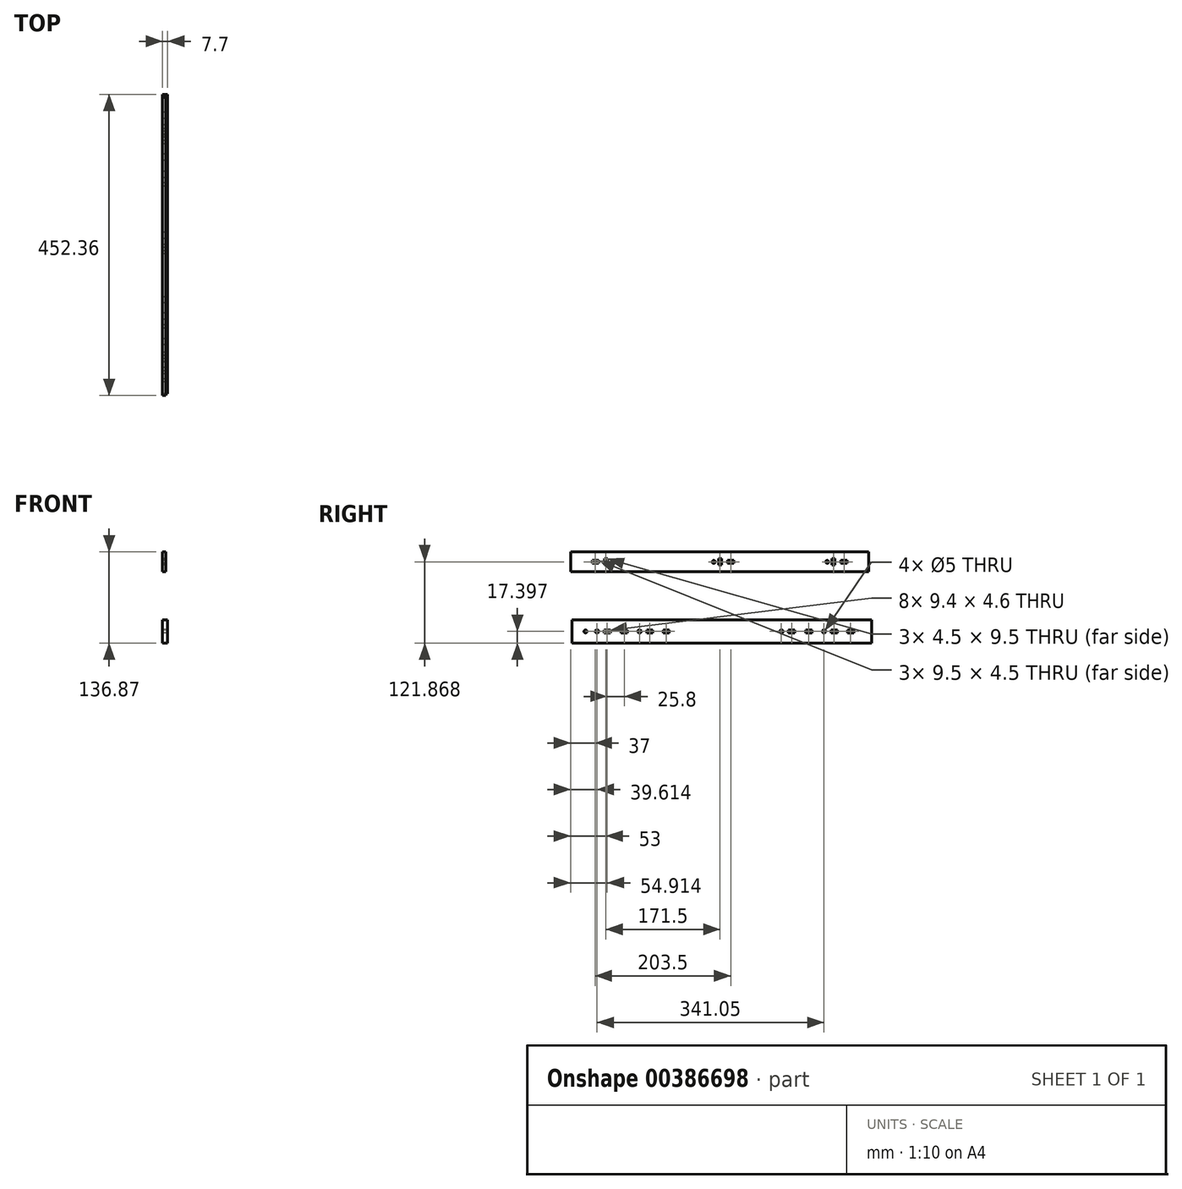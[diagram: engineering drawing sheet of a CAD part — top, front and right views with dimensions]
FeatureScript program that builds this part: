
annotation { "Feature Type Name" : "Feature", "Feature Type Description" : "" }
export const myFeature = defineFeature(function(context is Context, id is Id, definition is map)
    precondition{}
    {
        {
            var Q0;
            Q0=qCreatedBy(makeId("Right.planeOp"),FACE);
            var sketch = newSketch(context, id + "F0", { "sketchPlane" : qUnion([Q0])});
            skLineSegment(sketch, "E0.bottom", {"start": v(-266.34, -47.42) * mm, "end": v(183.66, -47.42) * mm});
            skLineSegment(sketch, "E0.top", {"start": v(-266.34, -82.22) * mm, "end": v(183.66, -82.22) * mm});
            skLineSegment(sketch, "E0.left", {"start": v(-266.34, -47.42) * mm, "end": v(-266.34, -82.22) * mm});
            skLineSegment(sketch, "E0.right", {"start": v(183.66, -47.42) * mm, "end": v(183.66, -82.22) * mm});
            skLineSegment(sketch, "E1", {"start": v(183.66, -64.82) * mm, "end": v(-266.34, -64.82) * mm, "construction": true});
            skCircle(sketch, "E2", {"center": v(111.96, -64.82) * mm, "radius": 2.5 * mm});
            skCircle(sketch, "E3", {"center": v(-229.09, -64.82) * mm, "radius": 2.5 * mm});
            skCircle(sketch, "E4", {"center": v(-165.09, -64.82) * mm, "radius": 2.5 * mm});
            skCircle(sketch, "E5", {"center": v(47.96, -64.82) * mm, "radius": 2.5 * mm});
            skCircle(sketch, "E6", {"center": v(-246.34, -64.82) * mm, "radius": 2.25 * mm});
            skLineSegment(sketch, "E7.bottom", {"start": v(131.96, -62.52) * mm, "end": v(122.56, -62.52) * mm});
            skLineSegment(sketch, "E7.top", {"start": v(131.96, -67.12) * mm, "end": v(122.56, -67.12) * mm});
            skLineSegment(sketch, "E7.left", {"start": v(131.96, -62.52) * mm, "end": v(131.96, -67.12) * mm});
            skLineSegment(sketch, "E7.right", {"start": v(122.56, -62.52) * mm, "end": v(122.56, -67.12) * mm});
            skPoint(sketch, "E7.middle", {"position": v(127.26, -64.82) * mm});
            skLineSegment(sketch, "E8.bottom", {"start": v(156.66, -62.52) * mm, "end": v(147.26, -62.52) * mm});
            skLineSegment(sketch, "E8.top", {"start": v(156.66, -67.12) * mm, "end": v(147.26, -67.12) * mm});
            skLineSegment(sketch, "E8.left", {"start": v(156.66, -62.52) * mm, "end": v(156.66, -67.12) * mm});
            skLineSegment(sketch, "E8.right", {"start": v(147.26, -62.52) * mm, "end": v(147.26, -67.12) * mm});
            skPoint(sketch, "E8.middle", {"position": v(151.96, -64.82) * mm});
            skLineSegment(sketch, "E9.bottom", {"start": v(67.96, -62.52) * mm, "end": v(58.56, -62.52) * mm});
            skLineSegment(sketch, "E9.top", {"start": v(67.96, -67.12) * mm, "end": v(58.56, -67.12) * mm});
            skLineSegment(sketch, "E9.left", {"start": v(67.96, -62.52) * mm, "end": v(67.96, -67.12) * mm});
            skLineSegment(sketch, "E9.right", {"start": v(58.56, -62.52) * mm, "end": v(58.56, -67.12) * mm});
            skPoint(sketch, "E9.middle", {"position": v(63.26, -64.82) * mm});
            skLineSegment(sketch, "E10.bottom", {"start": v(93.76, -62.52) * mm, "end": v(84.36, -62.52) * mm});
            skLineSegment(sketch, "E10.top", {"start": v(93.76, -67.12) * mm, "end": v(84.36, -67.12) * mm});
            skLineSegment(sketch, "E10.left", {"start": v(93.76, -62.52) * mm, "end": v(93.76, -67.12) * mm});
            skLineSegment(sketch, "E10.right", {"start": v(84.36, -62.52) * mm, "end": v(84.36, -67.12) * mm});
            skPoint(sketch, "E10.middle", {"position": v(89.06, -64.82) * mm});
            skLineSegment(sketch, "E11.bottom", {"start": v(-145.09, -62.52) * mm, "end": v(-154.49, -62.52) * mm});
            skLineSegment(sketch, "E11.top", {"start": v(-145.09, -67.12) * mm, "end": v(-154.49, -67.12) * mm});
            skLineSegment(sketch, "E11.left", {"start": v(-145.09, -62.52) * mm, "end": v(-145.09, -67.12) * mm});
            skLineSegment(sketch, "E11.right", {"start": v(-154.49, -62.52) * mm, "end": v(-154.49, -67.12) * mm});
            skPoint(sketch, "E11.middle", {"position": v(-149.79, -64.82) * mm});
            skLineSegment(sketch, "E12.bottom", {"start": v(-120.39, -62.52) * mm, "end": v(-129.79, -62.52) * mm});
            skLineSegment(sketch, "E12.top", {"start": v(-120.39, -67.12) * mm, "end": v(-129.79, -67.12) * mm});
            skLineSegment(sketch, "E12.left", {"start": v(-120.39, -62.52) * mm, "end": v(-120.39, -67.12) * mm});
            skLineSegment(sketch, "E12.right", {"start": v(-129.79, -62.52) * mm, "end": v(-129.79, -67.12) * mm});
            skPoint(sketch, "E12.middle", {"position": v(-125.09, -64.82) * mm});
            skLineSegment(sketch, "E13.bottom", {"start": v(-209.09, -62.52) * mm, "end": v(-218.49, -62.52) * mm});
            skLineSegment(sketch, "E13.top", {"start": v(-209.09, -67.12) * mm, "end": v(-218.49, -67.12) * mm});
            skLineSegment(sketch, "E13.left", {"start": v(-209.09, -62.52) * mm, "end": v(-209.09, -67.12) * mm});
            skLineSegment(sketch, "E13.right", {"start": v(-218.49, -62.52) * mm, "end": v(-218.49, -67.12) * mm});
            skPoint(sketch, "E13.middle", {"position": v(-213.79, -64.82) * mm});
            skLineSegment(sketch, "E14.bottom", {"start": v(-183.29, -62.52) * mm, "end": v(-192.69, -62.52) * mm});
            skLineSegment(sketch, "E14.top", {"start": v(-183.29, -67.12) * mm, "end": v(-192.69, -67.12) * mm});
            skLineSegment(sketch, "E14.left", {"start": v(-183.29, -62.52) * mm, "end": v(-183.29, -67.12) * mm});
            skLineSegment(sketch, "E14.right", {"start": v(-192.69, -62.52) * mm, "end": v(-192.69, -67.12) * mm});
            skPoint(sketch, "E14.middle", {"position": v(-187.99, -64.82) * mm});
            skSolve(sketch);
        }
        {
            var Q0;
            Q0=qCreatedBy(makeId("Right.planeOp"),FACE);
            var sketch = newSketch(context, id + "F1", { "sketchPlane" : qUnion([Q0])});
            skLineSegment(sketch, "E15.bottom", {"start": v(-268.7, 54.65) * mm, "end": v(179.3, 54.65) * mm});
            skLineSegment(sketch, "E15.top", {"start": v(-268.7, 24.65) * mm, "end": v(179.3, 24.65) * mm});
            skLineSegment(sketch, "E15.left", {"start": v(-268.7, 54.65) * mm, "end": v(-268.7, 24.65) * mm});
            skLineSegment(sketch, "E15.right", {"start": v(179.3, 54.65) * mm, "end": v(179.3, 24.65) * mm});
            skLineSegment(sketch, "E16", {"start": v(-268.7, 39.65) * mm, "end": v(179.3, 39.65) * mm, "construction": true});
            skCircle(sketch, "E17", {"center": v(116.8, 39.65) * mm, "radius": 2.25 * mm});
            skCircle(sketch, "E18", {"center": v(-53.7, 39.65) * mm, "radius": 2.25 * mm});
            skCircle(sketch, "E19", {"center": v(-206.2, 39.65) * mm, "radius": 2.25 * mm});
            skLineSegment(sketch, "E20.bottom", {"start": v(-213.45, 44.4) * mm, "end": v(-217.95, 44.4) * mm});
            skLineSegment(sketch, "E20.top", {"start": v(-213.45, 34.9) * mm, "end": v(-217.95, 34.9) * mm});
            skLineSegment(sketch, "E20.left", {"start": v(-213.45, 44.4) * mm, "end": v(-213.45, 34.9) * mm});
            skLineSegment(sketch, "E20.right", {"start": v(-217.95, 44.4) * mm, "end": v(-217.95, 34.9) * mm});
            skPoint(sketch, "E20.middle", {"position": v(-215.7, 39.65) * mm});
            skLineSegment(sketch, "E21.bottom", {"start": v(-226.95, 37.4) * mm, "end": v(-236.45, 37.4) * mm});
            skLineSegment(sketch, "E21.top", {"start": v(-226.95, 41.9) * mm, "end": v(-236.45, 41.9) * mm});
            skLineSegment(sketch, "E21.left", {"start": v(-226.95, 37.4) * mm, "end": v(-226.95, 41.9) * mm});
            skLineSegment(sketch, "E21.right", {"start": v(-236.45, 37.4) * mm, "end": v(-236.45, 41.9) * mm});
            skPoint(sketch, "E21.middle", {"position": v(-231.7, 39.65) * mm});
            skLineSegment(sketch, "E22.bottom", {"start": v(-41.95, 34.9) * mm, "end": v(-46.45, 34.9) * mm});
            skLineSegment(sketch, "E22.top", {"start": v(-41.95, 44.4) * mm, "end": v(-46.45, 44.4) * mm});
            skLineSegment(sketch, "E22.left", {"start": v(-41.95, 34.9) * mm, "end": v(-41.95, 44.4) * mm});
            skLineSegment(sketch, "E22.right", {"start": v(-46.45, 34.9) * mm, "end": v(-46.45, 44.4) * mm});
            skPoint(sketch, "E22.middle", {"position": v(-44.2, 39.65) * mm});
            skLineSegment(sketch, "E23.bottom", {"start": v(128.55, 34.9) * mm, "end": v(124.05, 34.9) * mm});
            skLineSegment(sketch, "E23.top", {"start": v(128.55, 44.4) * mm, "end": v(124.05, 44.4) * mm});
            skLineSegment(sketch, "E23.left", {"start": v(128.55, 34.9) * mm, "end": v(128.55, 44.4) * mm});
            skLineSegment(sketch, "E23.right", {"start": v(124.05, 34.9) * mm, "end": v(124.05, 44.4) * mm});
            skPoint(sketch, "E23.middle", {"position": v(126.3, 39.65) * mm});
            skLineSegment(sketch, "E24.bottom", {"start": v(147.05, 41.9) * mm, "end": v(137.55, 41.9) * mm});
            skLineSegment(sketch, "E24.top", {"start": v(147.05, 37.4) * mm, "end": v(137.55, 37.4) * mm});
            skLineSegment(sketch, "E24.left", {"start": v(147.05, 41.9) * mm, "end": v(147.05, 37.4) * mm});
            skLineSegment(sketch, "E24.right", {"start": v(137.55, 41.9) * mm, "end": v(137.55, 37.4) * mm});
            skPoint(sketch, "E24.middle", {"position": v(142.3, 39.65) * mm});
            skLineSegment(sketch, "E25.bottom", {"start": v(-23.45, 41.9) * mm, "end": v(-32.95, 41.9) * mm});
            skLineSegment(sketch, "E25.top", {"start": v(-23.45, 37.4) * mm, "end": v(-32.95, 37.4) * mm});
            skLineSegment(sketch, "E25.left", {"start": v(-23.45, 41.9) * mm, "end": v(-23.45, 37.4) * mm});
            skLineSegment(sketch, "E25.right", {"start": v(-32.95, 41.9) * mm, "end": v(-32.95, 37.4) * mm});
            skPoint(sketch, "E25.middle", {"position": v(-28.2, 39.65) * mm});
            skSolve(sketch);
        }
        {
            var Q0;
            Q0=qSketchRegion(id+"F0",true);
            extrude(context, id + "F2", {"entities" : qUnion([Q0]), "depth" : 7.7 * mm});
        }
        {
            var Q0;
            Q0=qSketchRegion(id+"F1",true);
            extrude(context, id + "F3", {"entities" : qUnion([Q0]), "depth" : 5 * mm});
        }
    });
